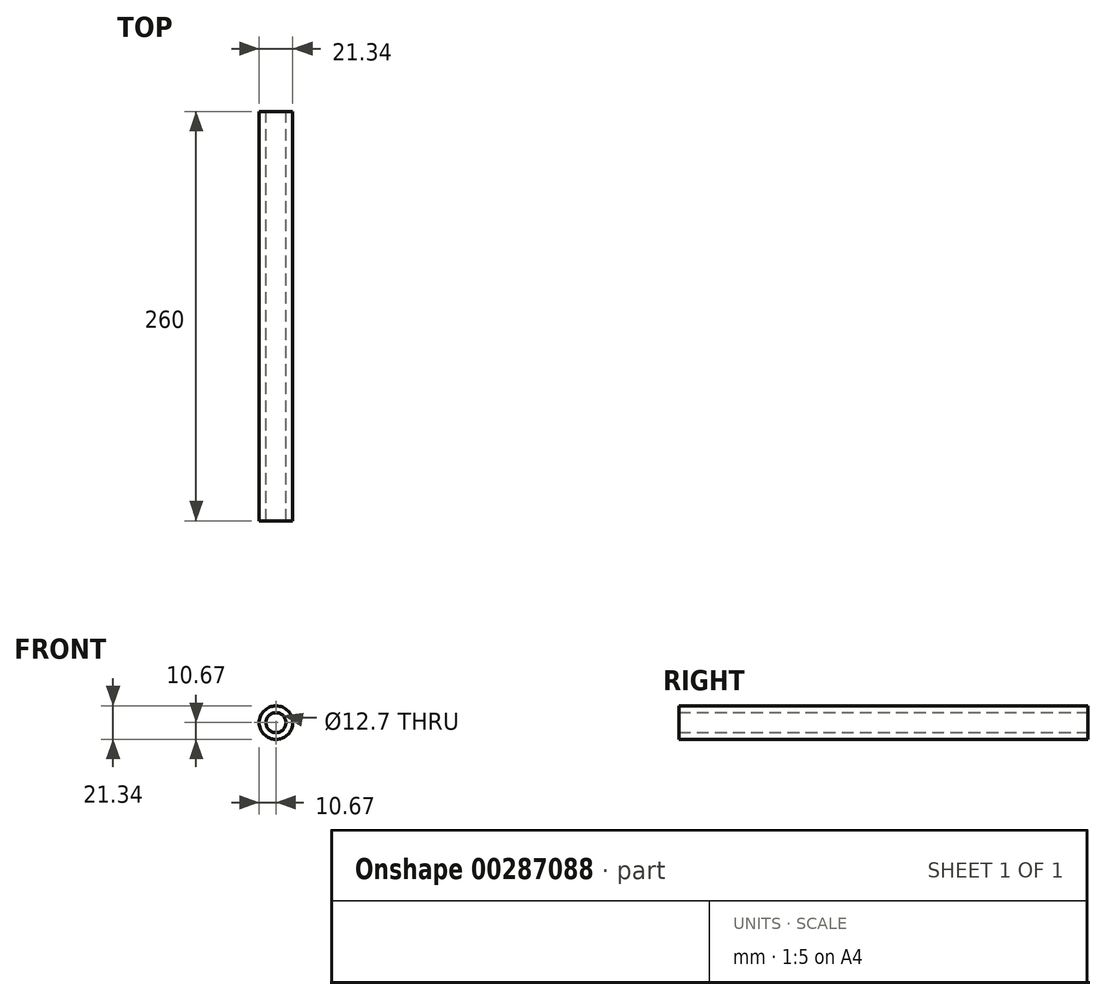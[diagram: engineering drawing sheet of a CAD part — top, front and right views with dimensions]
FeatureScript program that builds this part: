
annotation { "Feature Type Name" : "Feature", "Feature Type Description" : "" }
export const myFeature = defineFeature(function(context is Context, id is Id, definition is map)
    precondition{}
    {
        {
            var Q0;
            Q0=qCreatedBy(makeId("Front.planeOp"),FACE);
            var sketch = newSketch(context, id + "F0", { "sketchPlane" : qUnion([Q0])});
            skCircle(sketch, "E0", {"center": v(0, 0) * mm, "radius": 10.67 * mm});
            skCircle(sketch, "E1", {"center": v(0, 0) * mm, "radius": 6.35 * mm});
            skSolve(sketch);
        }
        {
            var Q0;
            Q0=qSketchRegion(id+"F0",true);
            extrude(context, id + "F1", {"entities" : qUnion([Q0]), "depth" : 260 * mm});
        }
    });
